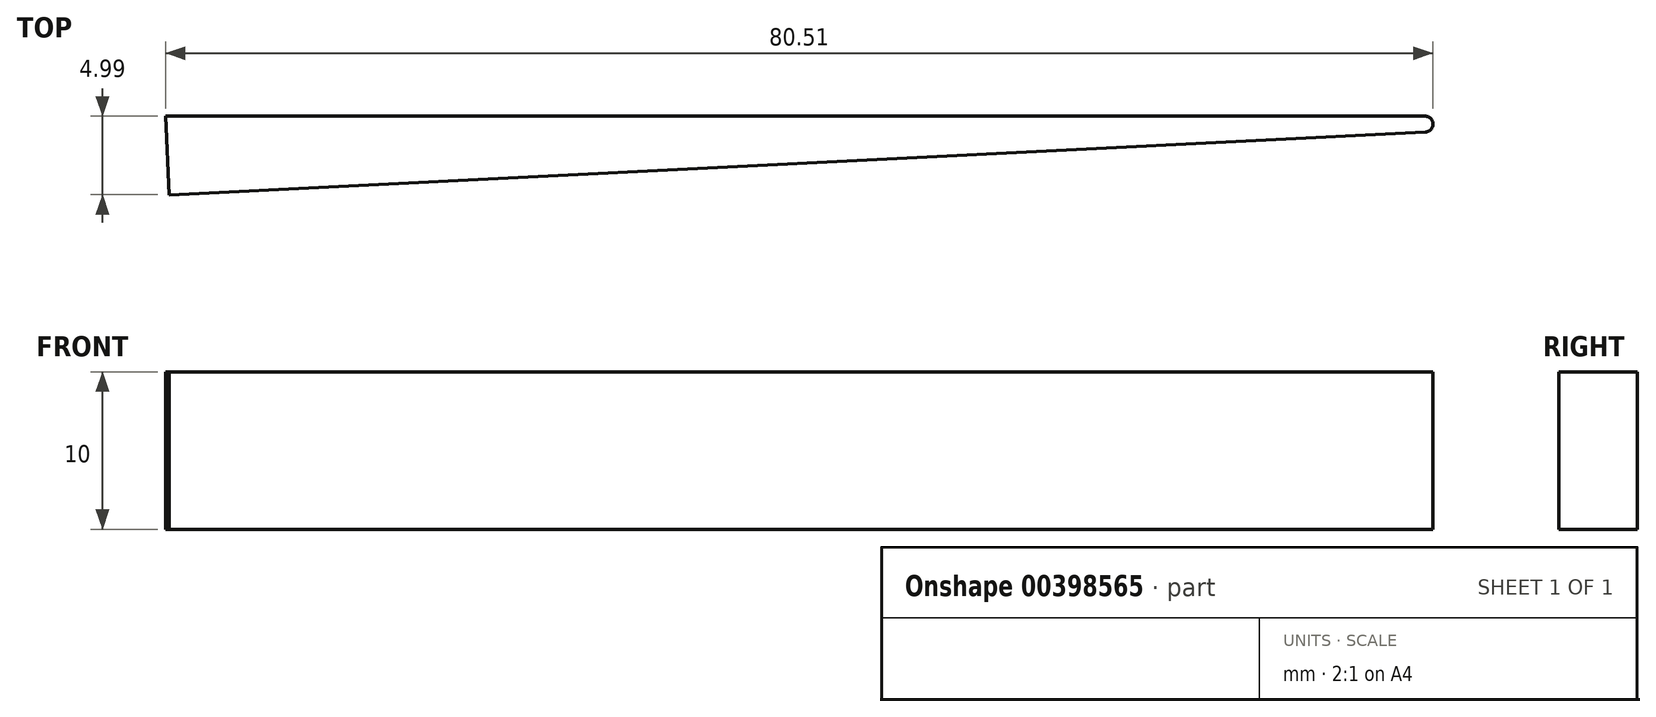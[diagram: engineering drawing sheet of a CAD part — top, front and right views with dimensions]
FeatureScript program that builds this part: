
annotation { "Feature Type Name" : "Feature", "Feature Type Description" : "" }
export const myFeature = defineFeature(function(context is Context, id is Id, definition is map)
    precondition{}
    {
        {
            var Q0;
            Q0=qCreatedBy(makeId("Top.planeOp"),FACE);
            var sketch = newSketch(context, id + "F0", { "sketchPlane" : qUnion([Q0])});
            skLineSegment(sketch, "E0", {"start": v(-47.4, 0) * mm, "end": v(52.6, 0) * mm});
            skLineSegment(sketch, "E1", {"start": v(52.6, 0) * mm, "end": v(-47.15, -5) * mm});
            skLineSegment(sketch, "E2", {"start": v(-47.15, -5) * mm, "end": v(-47.4, 0) * mm});
            skSolve(sketch);
        }
        {
            var Q0;
            Q0 = qSketchRegion(id + "F0", true);
            extrude(context, id + "F1", {"entities" : qUnion([Q0]), "depth" : 10 * mm});
        }
        {
            var Q0;
            Q0=makeQuery(id+"F1.opExtrude","SWEPT_EDGE",EDGE,{"disambiguationData":[OSD([sQuery(id+"F0.wireOp",EDGE,"E0"),sQuery(id+"F0.wireOp",EDGE,"E1")])]});
            fillet(context, id + "F2", {"entities" : qUnion([Q0]), "radius" : .5 * mm, "tangentPropagation" : true, "allowEdgeOverflow" : false});
        }
    });
